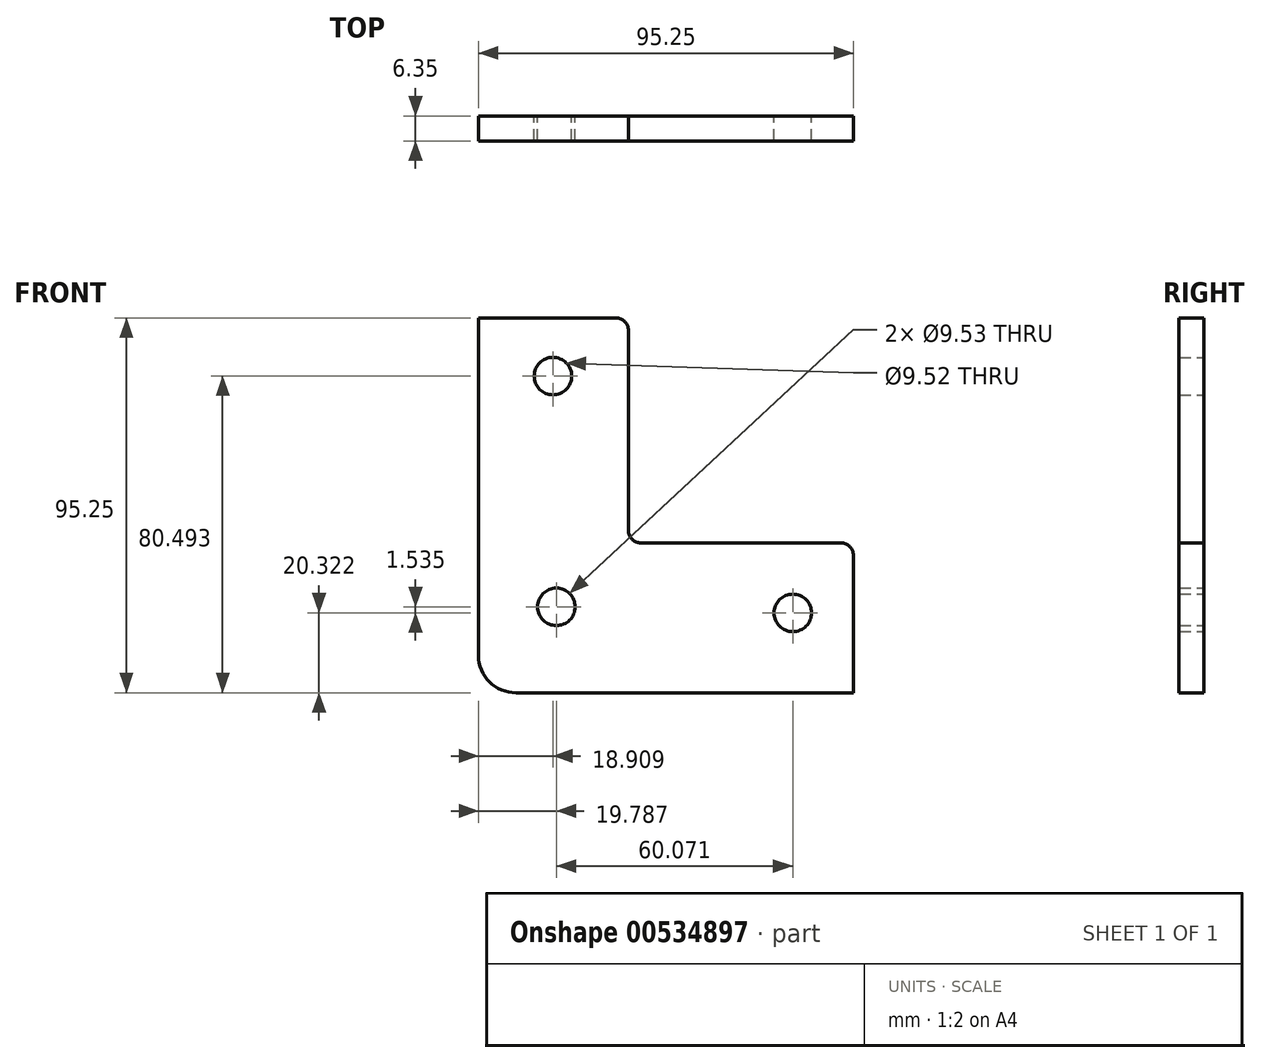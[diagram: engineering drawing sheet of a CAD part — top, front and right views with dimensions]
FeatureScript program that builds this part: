
annotation { "Feature Type Name" : "Feature", "Feature Type Description" : "" }
export const myFeature = defineFeature(function(context is Context, id is Id, definition is map)
    precondition{}
    {
        {
            var Q0;
            Q0=qCreatedBy(makeId("Front.planeOp"),FACE);
            var sketch = newSketch(context, id + "F0", { "sketchPlane" : qUnion([Q0])});
            skLineSegment(sketch, "E0", {"start": v(-65.45, 36.73) * mm, "end": v(-65.45, -49) * mm});
            skLineSegment(sketch, "E1", {"start": v(-55.92, -58.52) * mm, "end": v(29.8, -58.52) * mm});
            skLineSegment(sketch, "E2", {"start": v(29.8, -58.52) * mm, "end": v(29.8, -23.6) * mm});
            skLineSegment(sketch, "E3", {"start": v(26.63, -20.42) * mm, "end": v(-24.17, -20.42) * mm});
            skLineSegment(sketch, "E4", {"start": v(-27.35, -17.25) * mm, "end": v(-27.35, 33.55) * mm});
            skLineSegment(sketch, "E5", {"start": v(-65.45, 36.73) * mm, "end": v(-30.52, 36.73) * mm});
            skPoint(sketch, "E6.visualSharp", {"position": v(-65.45, 36.73) * mm});
            skLineSegment(sketch, "E6.filletArc", {"start": v(-65.45, 36.73) * mm, "end": v(-65.45, 36.73) * mm});
            skPoint(sketch, "E7.visualSharp", {"position": v(-27.35, 36.73) * mm});
            skArc(sketch, "E7.filletArc", {"start": v(-27.35, 33.55) * mm, "mid": v(-28.28, 35.8) * mm, "end": v(-30.52, 36.73) * mm});
            skPoint(sketch, "E8.visualSharp", {"position": v(-27.35, -20.42) * mm});
            skArc(sketch, "E8.filletArc", {"start": v(-27.35, -17.25) * mm, "mid": v(-26.42, -19.5) * mm, "end": v(-24.17, -20.42) * mm});
            skPoint(sketch, "E9.visualSharp", {"position": v(29.8, -20.42) * mm});
            skArc(sketch, "E9.filletArc", {"start": v(29.8, -23.6) * mm, "mid": v(28.87, -21.35) * mm, "end": v(26.63, -20.42) * mm});
            skPoint(sketch, "E10.visualSharp", {"position": v(-65.45, -58.52) * mm});
            skArc(sketch, "E10.filletArc", {"start": v(-65.45, -49) * mm, "mid": v(-62.66, -55.73) * mm, "end": v(-55.92, -58.52) * mm});
            skCircle(sketch, "E11", {"center": v(-46.54, 21.97) * mm, "radius": 4.76 * mm});
            skCircle(sketch, "E12", {"center": v(-45.66, -36.66) * mm, "radius": 4.76 * mm});
            skCircle(sketch, "E13", {"center": v(14.4, -38.2) * mm, "radius": 4.76 * mm});
            skSolve(sketch);
        }
        {
            var Q0;
            Q0 = qSketchRegion(id + "F0", true);
            extrude(context, id + "F1", {"entities" : qUnion([Q0]), "depth" : 6.35 * mm, "offsetDistance" : 25.4 * mm});
        }
    });
